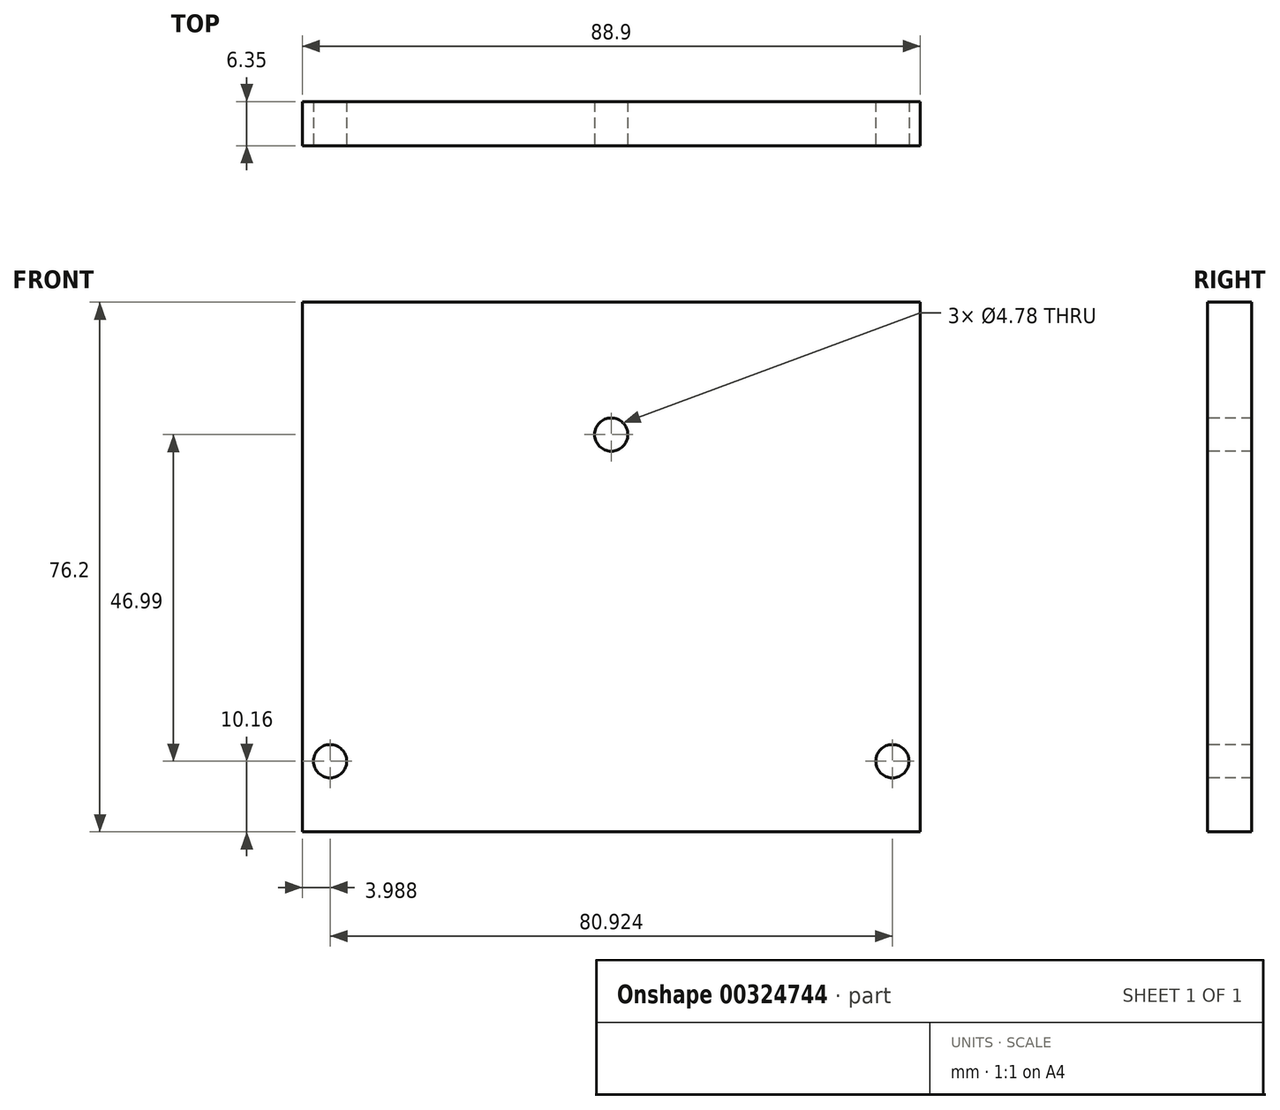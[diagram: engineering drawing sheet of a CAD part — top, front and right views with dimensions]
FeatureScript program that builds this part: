
annotation { "Feature Type Name" : "Feature", "Feature Type Description" : "" }
export const myFeature = defineFeature(function(context is Context, id is Id, definition is map)
    precondition{}
    {
        {
            var Q0;
            Q0=qCreatedBy(makeId("Front.planeOp"),FACE);
            var sketch = newSketch(context, id + "F0", { "sketchPlane" : qUnion([Q0])});
            skLineSegment(sketch, "E0.bottom", {"start": v(-44.45, 0) * mm, "end": v(44.45, 0) * mm});
            skLineSegment(sketch, "E0.top", {"start": v(-44.45, 76.2) * mm, "end": v(44.45, 76.2) * mm});
            skLineSegment(sketch, "E0.left", {"start": v(-44.45, 0) * mm, "end": v(-44.45, 76.2) * mm});
            skLineSegment(sketch, "E0.right", {"start": v(44.45, 0) * mm, "end": v(44.45, 76.2) * mm});
            skCircle(sketch, "E1", {"center": v(0, 57.15) * mm, "radius": 2.39 * mm});
            skCircle(sketch, "E2", {"center": v(-40.46, 10.16) * mm, "radius": 2.39 * mm});
            skCircle(sketch, "E3.MirrorC", {"center": v(40.46, 10.16) * mm, "radius": 2.39 * mm});
            skSolve(sketch);
        }
        {
            var Q0;
            Q0=makeQuery(id+"F0.imprint","IMPRINT",FACE,{"disambiguationData":[TD([[makeQuery(id+"F0.imprint","IMPRINT",EDGE,{"derivedFrom":sQuery(id+"F0.wireOp",EDGE,"E0.bottom")}),1.0]])]});
            extrude(context, id + "F1", {"entities" : qUnion([Q0]), "oppositeDirection" : true, "depth" : 6.35 * mm, "offsetDistance" : 25.4 * mm});
        }
    });
